# Revit family: Zumtobel LF3 DI
name_source: partatom
category: Lighting Fixtures
revit_build: Autodesk Revit 2016 (Build: 20150220_1215(x64)
units: mm (PartAtom-declared; Revit-internal decimal feet)

## family parameters
Cut with Voids When Loaded = No
Host = Face
Light Source = Yes
OmniClass Number = 23.80.70.11
OmniClass Title = Luminaries for Internal Lighting
Part Type = Normal
Room Calculation Point = No
Round Connector Dimension = Use Diameter
Shared = No

## types (2) — shared parameters
Assembly Code = D5020200
Body = ZG_Metal_White
Color Filter = 16777215
Cover = ZG_Lamp_Self_llumination
Description = Pendant LED luminaire
Dimming Lamp Color Temperature Shift = <None>
Emit Shape Visible in Rendering = No
Emit from Rectangle Length = 267 mm  [stored 0.875984 ft]
Height = 50 mm  [stored 0.164042 ft]
Lamp = LED
Manufacturer = Zumtobel Lighting
Tilt Angle = -90.00°
Voltage = 230 V
Width = 267 mm  [stored 0.875984 ft]
zero-valued in all types: Default Elevation

## per-type parameters (varying)
| type | Apparent Load | Emit from Rectangle Width | Length | Model | Photometric Web File | URL |
| LF3 D/I L15 | 64 VA | 1446 mm | 1446 mm | 42186947 | 42186947_(IND_LEO1_I_D).IES | www.zumtobel.com/42186947 |
| LF3 D/I L12 | 53 VA | 1164 mm  [stored 3.8189 ft] | 1164 mm  [stored 3.8189 ft] | 42186946 | 42186946_(IND_LEO1_I_D).IES | www.zumtobel.com/42186946 |

note: [stored X ft] marks values corroborated as IEEE doubles in the binary element streams (Revit-internal decimal feet)

## geometry (parser evidence)
native form markers: Sweep x6
no freeform markers — native parametric forms only
